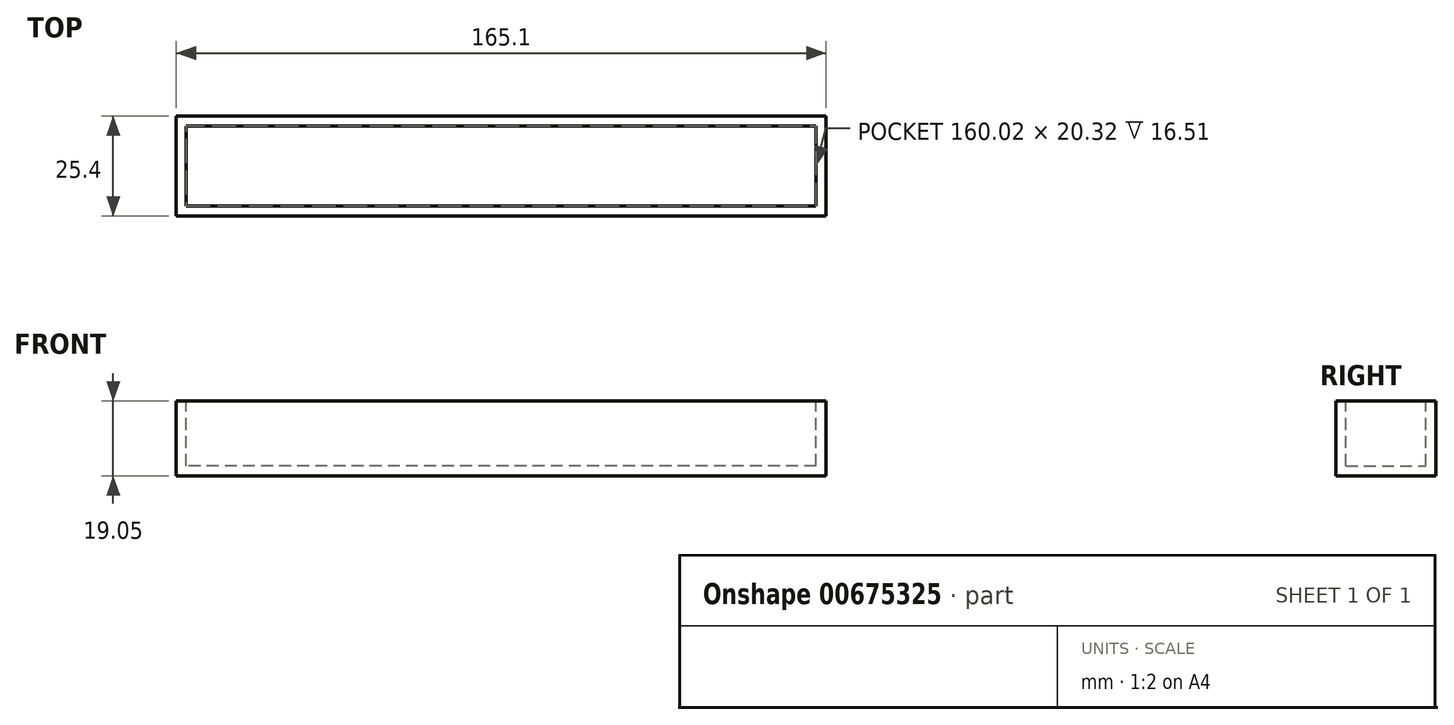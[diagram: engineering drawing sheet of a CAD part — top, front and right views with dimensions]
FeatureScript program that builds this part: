
annotation { "Feature Type Name" : "Feature", "Feature Type Description" : "" }
export const myFeature = defineFeature(function(context is Context, id is Id, definition is map)
    precondition{}
    {
        {
            var Q0;
            Q0=qCreatedBy(makeId("Front.planeOp"),FACE);
            var sketch = newSketch(context, id + "F0", { "sketchPlane" : qUnion([Q0])});
            skLineSegment(sketch, "E0.bottom", {"start": v(0, 0) * mm, "end": v(165.1, 0) * mm});
            skLineSegment(sketch, "E0.top", {"start": v(0, 19.05) * mm, "end": v(165.1, 19.05) * mm});
            skLineSegment(sketch, "E0.left", {"start": v(0, 0) * mm, "end": v(0, 19.05) * mm});
            skLineSegment(sketch, "E0.right", {"start": v(165.1, 0) * mm, "end": v(165.1, 19.05) * mm});
            skSolve(sketch);
        }
        {
            var Q0;
            Q0 = qSketchRegion(id + "F0", true);
            extrude(context, id + "F1", {"entities" : qUnion([Q0]), "depth" : 25.4 * mm, "offsetDistance" : 25.4 * mm});
        }
        {
            var Q0;
            Q0=makeQuery(id+"F1.opExtrude","SWEPT_FACE",FACE,{"disambiguationData":[OSD([sQuery(id+"F0.wireOp",EDGE,"E0.top")])]});
            var sketch = newSketch(context, id + "F2", { "sketchPlane" : qUnion([Q0])});
            skLineSegment(sketch, "E1.bottom", {"start": v(162.56, -22.86) * mm, "end": v(2.54, -22.86) * mm});
            skLineSegment(sketch, "E1.top", {"start": v(162.56, -2.54) * mm, "end": v(2.54, -2.54) * mm});
            skLineSegment(sketch, "E1.left", {"start": v(162.56, -22.86) * mm, "end": v(162.56, -2.54) * mm});
            skLineSegment(sketch, "E1.right", {"start": v(2.54, -22.86) * mm, "end": v(2.54, -2.54) * mm});
            skSolve(sketch);
        }
        {
            var Q0;
            Q0 = qSketchRegion(id + "F2", true);
            extrude(context, id + "F3", {"entities" : qUnion([Q0]), "operationType" : NewBodyOperationType.REMOVE, "oppositeDirection" : true, "depth" : 16.5 * mm, "offsetDistance" : 25.4 * mm});
        }
    });
